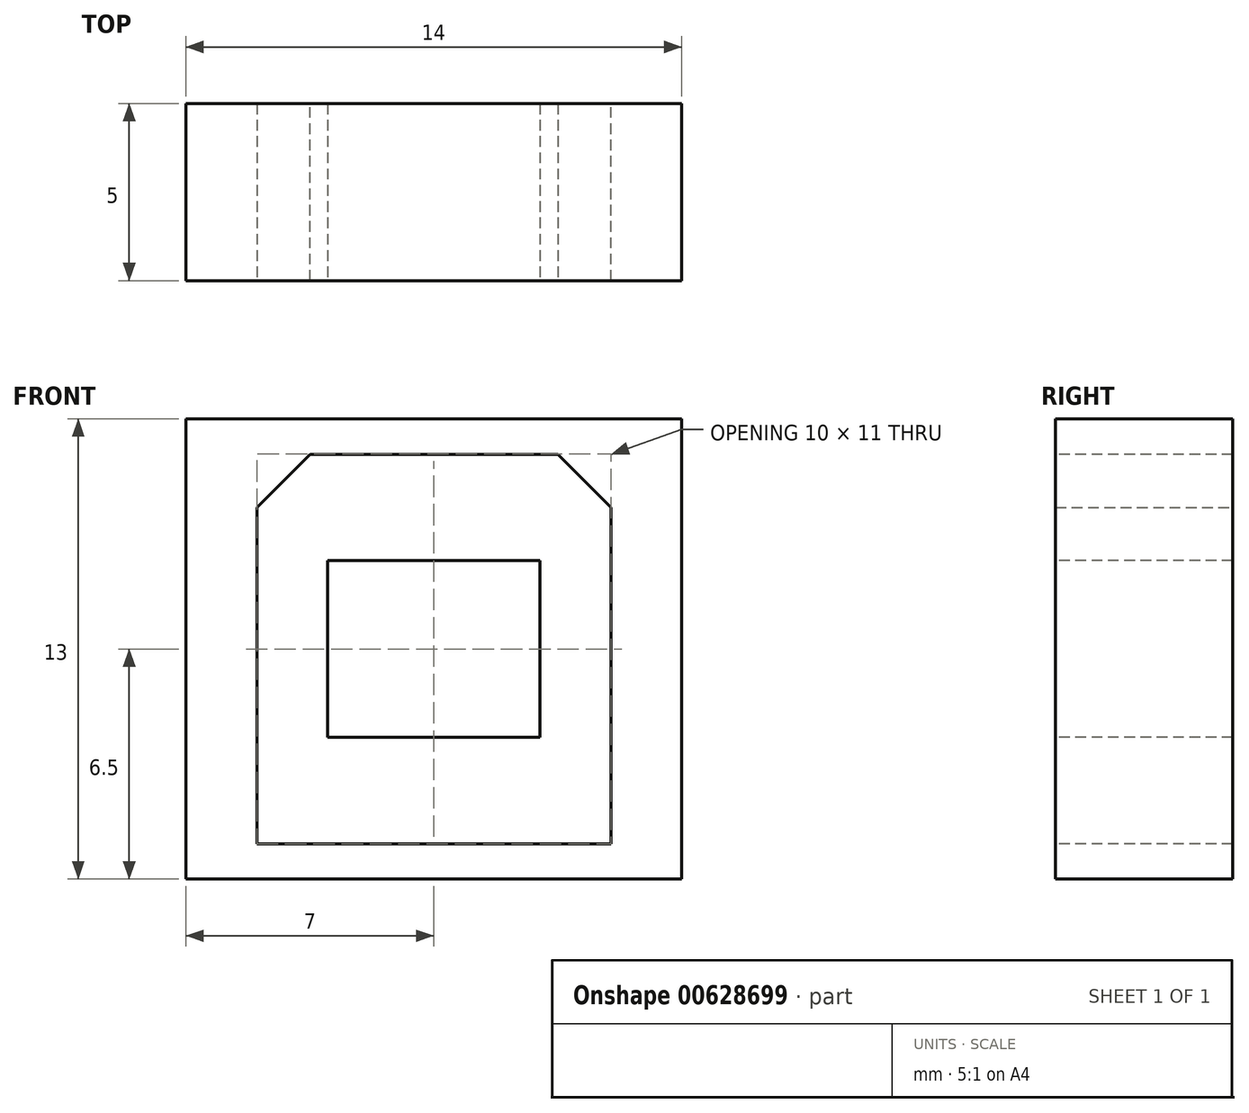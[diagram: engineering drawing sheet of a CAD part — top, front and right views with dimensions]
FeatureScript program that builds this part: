
annotation { "Feature Type Name" : "Feature", "Feature Type Description" : "" }
export const myFeature = defineFeature(function(context is Context, id is Id, definition is map)
    precondition{}
    {
        {
            var Q0;
            Q0=qCreatedBy(makeId("Front.planeOp"),FACE);
            var sketch = newSketch(context, id + "F0", { "sketchPlane" : qUnion([Q0])});
            skLineSegment(sketch, "E0.bottom", {"start": v(7, 6.5) * mm, "end": v(-7, 6.5) * mm});
            skLineSegment(sketch, "E0.top", {"start": v(7, -6.5) * mm, "end": v(-7, -6.5) * mm});
            skLineSegment(sketch, "E0.left", {"start": v(7, 6.5) * mm, "end": v(7, -6.5) * mm});
            skLineSegment(sketch, "E0.right", {"start": v(-7, 6.5) * mm, "end": v(-7, -6.5) * mm});
            skPoint(sketch, "E0.middle", {"position": v(0, 0) * mm});
            skSolve(sketch);
        }
        {
            var Q0;
            Q0 = qSketchRegion(id + "F0", true);
            extrude(context, id + "F1", {"entities" : qUnion([Q0]), "endBound" : BoundingType.SYMMETRIC, "depth" : 5 * mm, "offsetDistance" : 25 * mm});
        }
        {
            var Q0;
            Q0=makeQuery(id+"F1.opExtrude","CAP_FACE",FACE,{"disambiguationData":[OSD([sQuery(id+"F0.wireOp",EDGE,"E0.bottom"),sQuery(id+"F0.wireOp",EDGE,"E0.top"),sQuery(id+"F0.wireOp",EDGE,"E0.left"),sQuery(id+"F0.wireOp",EDGE,"E0.right")])],"isStart":false});
            var sketch = newSketch(context, id + "F2", { "sketchPlane" : qUnion([Q0])});
            skLineSegment(sketch, "E1.bottom", {"start": v(5, 5.5) * mm, "end": v(-5, 5.5) * mm});
            skLineSegment(sketch, "E1.top", {"start": v(5, -5.5) * mm, "end": v(-5, -5.5) * mm});
            skLineSegment(sketch, "E1.left", {"start": v(5, 5.5) * mm, "end": v(5, -5.5) * mm});
            skLineSegment(sketch, "E1.right", {"start": v(-5, 5.5) * mm, "end": v(-5, -5.5) * mm});
            skPoint(sketch, "E1.middle", {"position": v(0, 0) * mm});
            skLineSegment(sketch, "E2.bottom", {"start": v(3, -2.5) * mm, "end": v(-3, -2.5) * mm});
            skLineSegment(sketch, "E2.top", {"start": v(3, 2.5) * mm, "end": v(-3, 2.5) * mm});
            skLineSegment(sketch, "E2.left", {"start": v(3, -2.5) * mm, "end": v(3, 2.5) * mm});
            skLineSegment(sketch, "E2.right", {"start": v(-3, -2.5) * mm, "end": v(-3, 2.5) * mm});
            skSolve(sketch);
        }
        {
            var Q0;
            Q0=makeQuery(id+"F2.imprint","IMPRINT",FACE,{"disambiguationData":[TD([[makeQuery(id+"F2.imprint","IMPRINT",EDGE,{"derivedFrom":sQuery(id+"F2.wireOp",EDGE,"E1.bottom")}),1.0]])]});
            extrude(context, id + "F3", {"entities" : qUnion([Q0]), "operationType" : NewBodyOperationType.REMOVE, "endBound" : BoundingType.THROUGH_ALL, "oppositeDirection" : true, "depth" : 4 * mm, "offsetDistance" : 25 * mm});
        }
        {
            var Q0;
            Q0=makeQuery(id+"F3.boolean.opBoolean","COPY",EDGE,{"derivedFrom":makeQuery(id+"F3.opExtrude","SWEPT_EDGE",EDGE,{"disambiguationData":[OSD([sQuery(id+"F2.wireOp",EDGE,"E1.bottom"),sQuery(id+"F2.wireOp",EDGE,"E1.right")])]})});
            var Q1;
            Q1=makeQuery(id+"F3.boolean.opBoolean","COPY",EDGE,{"derivedFrom":makeQuery(id+"F3.opExtrude","SWEPT_EDGE",EDGE,{"disambiguationData":[OSD([sQuery(id+"F2.wireOp",EDGE,"E1.bottom"),sQuery(id+"F2.wireOp",EDGE,"E1.left")])]})});
            chamfer(context, id + "F4", {"entities" : qUnion([Q0, Q1]), "width" : 1.5 * mm, "tangentPropagation" : true});
        }
    });
